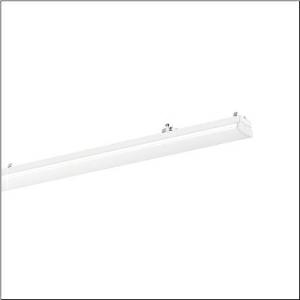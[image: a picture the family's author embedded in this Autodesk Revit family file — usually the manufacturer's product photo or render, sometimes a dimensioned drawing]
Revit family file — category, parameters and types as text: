
# Revit family: licross_r__11_recessed_opal_mo_51te1d7n48xg_2f8c
name_source: partatom
category: Lighting Fixtures
units: mm (PartAtom-declared; Revit-internal decimal feet)

## family parameters
Cut with Voids When Loaded = No
Host = Face
Light Source = No
Part Type = Normal
Room Calculation Point = No
Round Connector Dimension = Use Diameter
Shared = No

## types (1)
- Licross® 11 recessed opal MO (1 x LED, 8490 lm, 48.5 W, 4000K)
    Apparent Load = 49 VA
    CIE Flux Codes = 44 73 91 87 100
    Color Rendering = 80
    Color Temperature = 4000K
    Default Elevation = 1800 mm
    Description = Licross® 11 recessed opal MO, luminaire insert, of sheet steel, coil coated, white, length: 1.500mm, width: 76mm, height: 87mm, LED rated luminous flux: 8.490lm, light colour: 840, control gear: ON/OFF, with plug, 3-pole, with phase selection, mains connection: 220..240V, AC, 50/60Hz, rated input power: 49W, halogen-free wiring, primary optical cover: cover, of PMMA, light emission: direct with ceiling illumination distribution, primary light characteristic: symmetric, protection rating (complete): IP54, insulation class (complete): insulation class I (protective earthing), certification: CE, ENEC, VDE, UKCA, protection symbol: D if used in an environment with non-conductive dust loads with corresponding accessories, impact resistance: IK06, permissible ambient temperature for indoor applications: -35..+35°C, corresponds to IFS (International Featured Standards) requirements for safety and quality in the food industry, reducing of maximum allowable ambient temperature of 5°C with ceiling mounting, packaging unit: 1 piece
    Height = 83 mm
    Lamp = 1 x LED
    Lamp Light Flux = 8490 lm
    Lamp Power = 48.5 W
    Lamp count = 1
    Length = 1500 mm
    Luminous efficacy = 175 lm/W
    Manufacturer = Siteco
    ModVariant = No
    Model = 51TE1D7N48XG
    Mounting Place = Ceiling
    Mounting Type = Pendant
    Number of Poles = 1
    OnlyDefault = Yes
    Power Factor = 1
    Product Name = Licross® 11 recessed opal MO
    Product group = luminaire insert
    ProductGroupID = 902
    Protection Class = Protection class I
    Protection Degree = IP 54
    RLX_Detail_Level = 1
    RLX_Emergency_Light_Flux = 0 lm
    RLX_Emergency_Type = 0
    RLX_Emergency_Type_DB = No
    RlxData = <blob elided: 22973 chars, md5=6934b5ca>
    Socket = socket
    Standby Power = 0 W
    System Light Flux = 8490 lm
    System Power = 49 W
    Type Comments = Product without accessories
    Type Image = l_1313666.jpg
    URL = http://relux.com
    VarID = ---
    Voltage = 0 V
    Weight = 0.00 kg
    Width = 76 mm

## geometry (parser evidence)
native form markers: Blend x4, Sweep x15
no freeform markers — native parametric forms only
